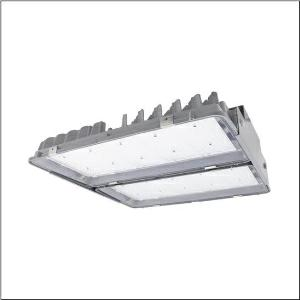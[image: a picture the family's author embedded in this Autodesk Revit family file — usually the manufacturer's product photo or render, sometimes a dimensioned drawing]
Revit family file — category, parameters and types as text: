
# Revit family: highbay_11xtreme_51hf81db4vma
name_source: partatom
category: Lighting Fixtures
units: mm (PartAtom-declared; Revit-internal decimal feet)

## family parameters
Cut with Voids When Loaded = No
Host = Face
Light Source = No
Part Type = Normal
Room Calculation Point = No
Round Connector Dimension = Use Diameter
Shared = No

## types (1)
- --- (1 x LED, 69400 lm, 380.2 W, 4000K)
    Apparent Load = 380 VA
    CIE Flux Codes = 88 96 99 100 100
    Color Rendering = 80
    Color Temperature = 4000K
    Default Elevation = 1800 mm
    Description = Highbay 11Xtreme, LED high bay luminaire, primary light control with lens, of PMMA, primary optical cover: cover, of toughened safety glass, light emission: direct distribution, primary light characteristic: symmetric, installation type: suspended mounting, surface-mounted, 2x LED module,for 1x 2x LED, rated luminous flux: 69.400lm, luminous efficacy: 183lm/W, light colour: 840, colour temperature: 4000K, with cable H07RN-F 5x 1.5mm², mains connection: 220..240V, AC, 50/60Hz, cable length: 1,5m, rated input power: 380W, luminaire housing, of diecast aluminium, partly coated, silver, length: 595mm, width: 560mm, height: 195mm, protection rating (complete): IP66, insulation class (complete): insulation class I (protective earthing), certification: CE, ENEC, UKCA, protection symbol: D, ball protection: ball impact resistant according to DIN VDE 0710 part 13 (with chain suspension), impact resistance: IK08, permissible operating ambient temperature: -25..+45°C, reducing of maximum allowable ambient temperature of 5°C with ceiling mounting, packaging unit: 1 piece
    Height = 157 mm
    Lamp = 1 x LED
    Lamp Light Flux = 69400 lm
    Lamp Power = 380.2 W
    Lamp count = 1
    Length = 593 mm
    Luminous efficacy = 183 lm/W
    Manufacturer = Siteco
    ModVariant = No
    Model = 51HF81DB4VMA
    Mounting Place = Ceiling
    Mounting Type = Pendant
    Number of Poles = 1
    OnlyDefault = Yes
    Power Factor = 1
    Product Name = Highbay 11Xtreme
    Product group = LED high bay luminaire
    ProductGroupID = 903
    Protection Class = Protection class I
    Protection Degree = IP 66
    RLX_Detail_Level = 1
    RLX_Emergency_Light_Flux = 0 lm
    RLX_Emergency_Type = 0
    RLX_Emergency_Type_DB = No
    RlxData = <blob elided: 33829 chars, md5=d773afb4>
    Socket = socket
    Standby Power = 0 W
    System Light Flux = 69402 lm
    System Power = 380 W
    Type Comments = factory setting: luminous flux: 100 % | dim-lin: 254 | 1257 mA
    Type Image = l_1258340.jpg
    URL = http://relux.com
    VarID = @adj_027897
    Voltage = 0 V
    Weight = 0.00 kg
    Width = 568 mm

## geometry (parser evidence)
native form markers: Blend x4, Sweep x10
no freeform markers — native parametric forms only
